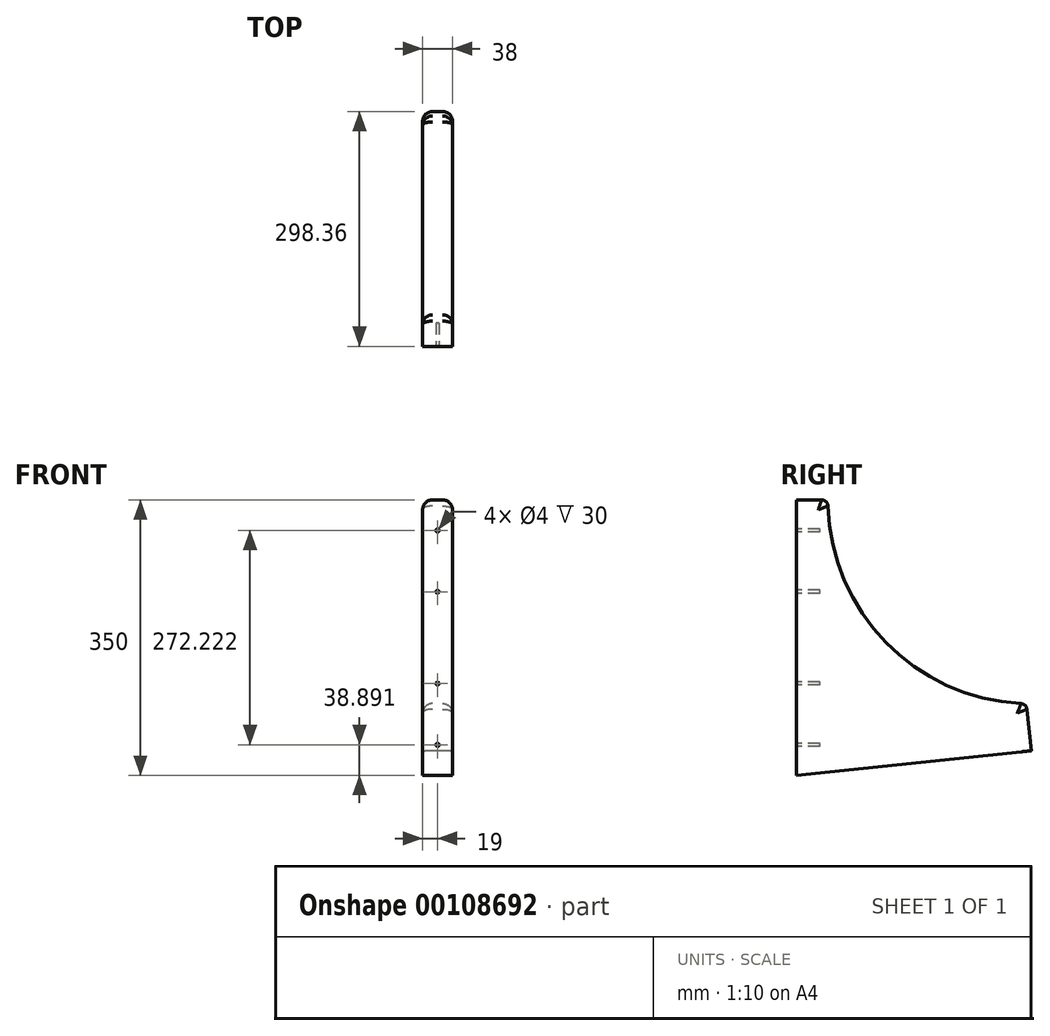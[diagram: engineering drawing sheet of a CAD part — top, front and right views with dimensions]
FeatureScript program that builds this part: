
annotation { "Feature Type Name" : "Feature", "Feature Type Description" : "" }
export const myFeature = defineFeature(function(context is Context, id is Id, definition is map)
    precondition{}
    {
        {
            var Q0;
            Q0=qCreatedBy(makeId("Right.planeOp"),FACE);
            var sketch = newSketch(context, id + "F0", { "sketchPlane" : qUnion([Q0])});
            skLineSegment(sketch, "E0", {"start": v(-102.8, -174.75) * mm, "end": v(-102.8, 175.25) * mm});
            skLineSegment(sketch, "E1", {"start": v(-102.8, 175.25) * mm, "end": v(-70.69, 175.25) * mm});
            skLineSegment(sketch, "E2", {"start": v(-102.8, -174.75) * mm, "end": v(290.45, -174.75) * mm, "construction": true});
            skLineSegment(sketch, "E3", {"start": v(-102.8, -174.75) * mm, "end": v(195.55, -143.39) * mm});
            skLineSegment(sketch, "E4", {"start": v(195.55, -143.39) * mm, "end": v(190, -90.6) * mm});
            skLineSegment(sketch, "E5", {"start": v(-62.8, 175.25) * mm, "end": v(196.26, 175.25) * mm, "construction": true});
            skLineSegment(sketch, "E6", {"start": v(196.26, 175.25) * mm, "end": v(196.26, -174.75) * mm, "construction": true});
            skArc(sketch, "E7", {"start": v(182.47, -83.45) * mm, "mid": v(10.95, -5.79) * mm, "end": v(-62.7, 167.5) * mm});
            skPoint(sketch, "E8.visualSharp", {"position": v(-62.8, 175.25) * mm});
            skArc(sketch, "E8.filletArc", {"start": v(-62.7, 167.5) * mm, "mid": v(-65.12, 173) * mm, "end": v(-70.69, 175.25) * mm});
            skPoint(sketch, "E9.visualSharp", {"position": v(189.28, -83.72) * mm});
            skArc(sketch, "E9.filletArc", {"start": v(190, -90.6) * mm, "mid": v(187.55, -85.63) * mm, "end": v(182.47, -83.45) * mm});
            skSolve(sketch);
        }
        {
            var Q0;
            Q0=makeQuery(id+"F0.imprint","IMPRINT",FACE,{"disambiguationData":[TD([[makeQuery(id+"F0.imprint","IMPRINT",EDGE,{"derivedFrom":sQuery(id+"F0.wireOp",EDGE,"E0")}),-1.0]])]});
            extrude(context, id + "F1", {"entities" : qUnion([Q0]), "depth" : 38 * mm, "symmetric" : true});
        }
        {
            var Q0;
            Q0=makeQuery(id+"F1.opExtrude","SWEPT_FACE",FACE,{"disambiguationData":[OSD([sQuery(id+"F0.wireOp",EDGE,"E0")])]});
            var sketch = newSketch(context, id + "F2", { "sketchPlane" : qUnion([Q0])});
            skLineSegment(sketch, "E10.0", {"start": v(19, 175.25) * mm, "end": v(-19, 175.25) * mm, "construction": true});
            skLineSegment(sketch, "E11.0", {"start": v(-19, -174.75) * mm, "end": v(-19, 175.25) * mm, "construction": true});
            skLineSegment(sketch, "E12.0", {"start": v(19, -174.75) * mm, "end": v(19, 175.25) * mm, "construction": true});
            skLineSegment(sketch, "E13.0", {"start": v(19, -174.75) * mm, "end": v(-19, -174.75) * mm, "construction": true});
            skLineSegment(sketch, "E14", {"start": v(0, 175.25) * mm, "end": v(0, 136.36) * mm, "construction": true});
            skLineSegment(sketch, "E15", {"start": v(0, 136.36) * mm, "end": v(0, 97.47) * mm, "construction": true});
            skLineSegment(sketch, "E16", {"start": v(0, 97.47) * mm, "end": v(0, 58.59) * mm, "construction": true});
            skLineSegment(sketch, "E17", {"start": v(0, 58.59) * mm, "end": v(0, 19.7) * mm, "construction": true});
            skLineSegment(sketch, "E18", {"start": v(0, 19.7) * mm, "end": v(0, -19.2) * mm, "construction": true});
            skLineSegment(sketch, "E19", {"start": v(0, -19.2) * mm, "end": v(0, -58.08) * mm, "construction": true});
            skLineSegment(sketch, "E20", {"start": v(0, -58.08) * mm, "end": v(0, -96.97) * mm, "construction": true});
            skLineSegment(sketch, "E21", {"start": v(0, -96.97) * mm, "end": v(0, -135.86) * mm, "construction": true});
            skLineSegment(sketch, "E22", {"start": v(0, -135.86) * mm, "end": v(0, -174.75) * mm, "construction": true});
            skCircle(sketch, "E23", {"center": v(0, 136.36) * mm, "radius": 2 * mm});
            skCircle(sketch, "E24", {"center": v(0, -135.86) * mm, "radius": 2 * mm});
            skCircle(sketch, "E25", {"center": v(0, 58.59) * mm, "radius": 2 * mm});
            skCircle(sketch, "E26", {"center": v(0, -58.08) * mm, "radius": 2 * mm});
            skSolve(sketch);
        }
        {
            var Q0;
            Q0=makeQuery(id+"F2.imprint","IMPRINT",FACE,{"disambiguationData":[TD([[makeQuery(id+"F2.imprint","IMPRINT",EDGE,{"derivedFrom":sQuery(id+"F2.wireOp",EDGE,"E23")}),1.0]])]});
            var Q1;
            Q1=makeQuery(id+"F2.imprint","IMPRINT",FACE,{"disambiguationData":[TD([[makeQuery(id+"F2.imprint","IMPRINT",EDGE,{"derivedFrom":sQuery(id+"F2.wireOp",EDGE,"E25")}),1.0]])]});
            var Q2;
            Q2=makeQuery(id+"F2.imprint","IMPRINT",FACE,{"disambiguationData":[TD([[makeQuery(id+"F2.imprint","IMPRINT",EDGE,{"derivedFrom":sQuery(id+"F2.wireOp",EDGE,"E26")}),1.0]])]});
            var Q3;
            Q3=makeQuery(id+"F2.imprint","IMPRINT",FACE,{"disambiguationData":[TD([[makeQuery(id+"F2.imprint","IMPRINT",EDGE,{"derivedFrom":sQuery(id+"F2.wireOp",EDGE,"E24")}),1.0]])]});
            extrude(context, id + "F3", {"entities" : qUnion([Q0, Q1, Q2, Q3]), "operationType" : NewBodyOperationType.REMOVE, "oppositeDirection" : true, "depth" : 30 * mm});
        }
        {
            var Q0;
            Q0=makeQuery(id+"F1.opExtrude","CAP_EDGE",EDGE,{"disambiguationData":[OSD([sQuery(id+"F0.wireOp",EDGE,"E7")])],"isStart":true});
            var Q1;
            Q1=makeQuery(id+"F1.opExtrude","CAP_EDGE",EDGE,{"disambiguationData":[OSD([sQuery(id+"F0.wireOp",EDGE,"E7")])],"isStart":false});
            fillet(context, id + "F4", {"entities" : qUnion([Q0, Q1]), "radius" : 12.5 * mm, "tangentPropagation" : true, "allowEdgeOverflow" : false});
        }
    });
